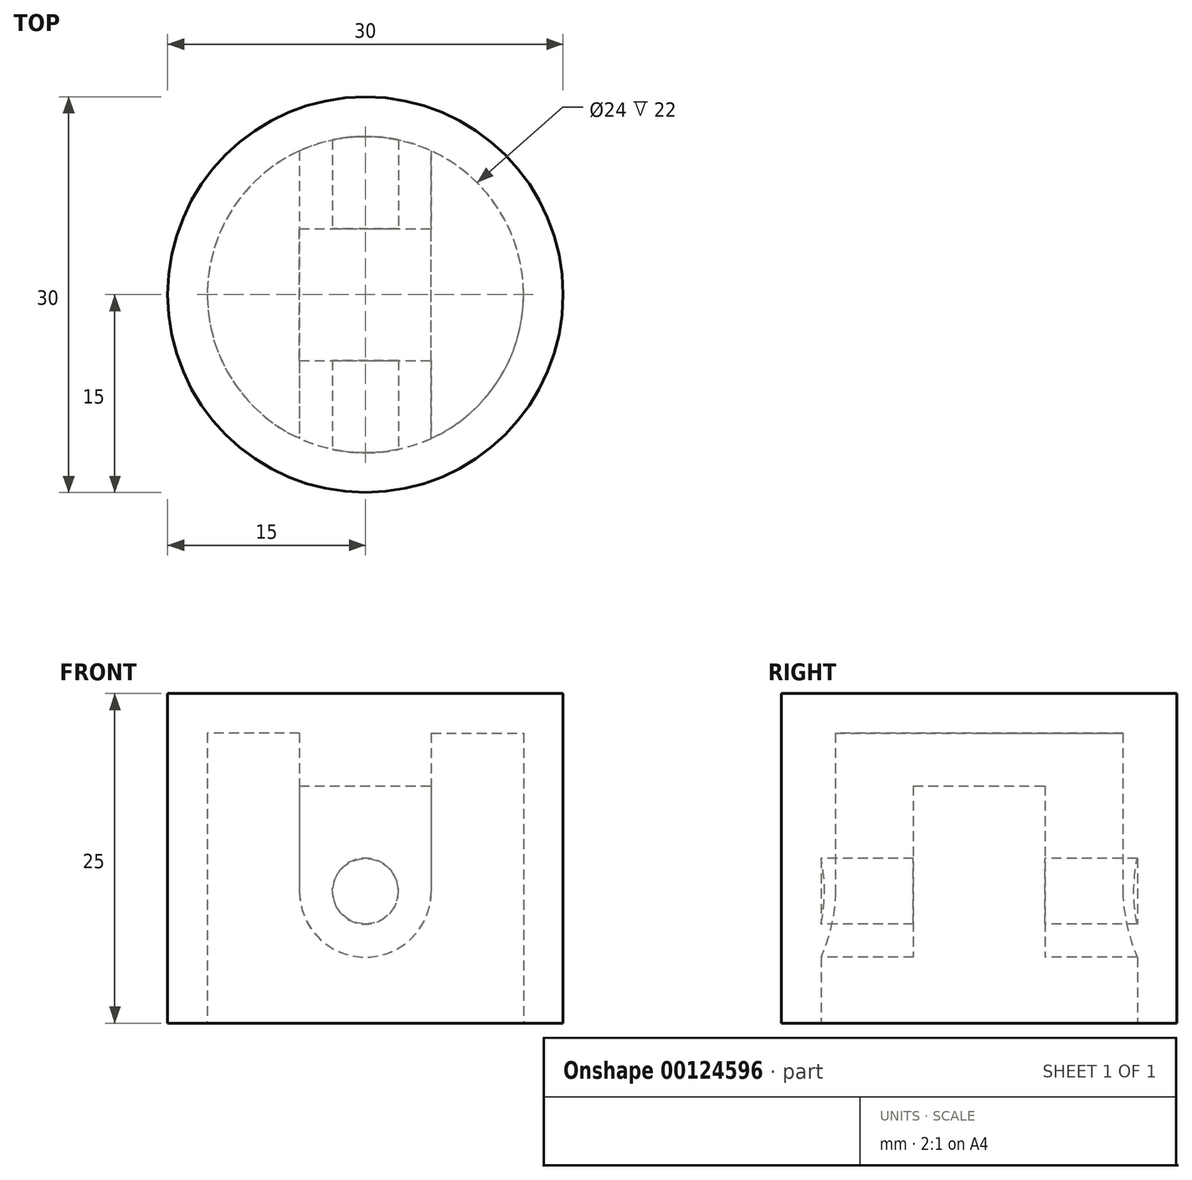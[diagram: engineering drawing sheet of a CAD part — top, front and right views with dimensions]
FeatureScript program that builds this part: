
annotation { "Feature Type Name" : "Feature", "Feature Type Description" : "" }
export const myFeature = defineFeature(function(context is Context, id is Id, definition is map)
    precondition{}
    {
        {
            var Q0;
            Q0=qCreatedBy(makeId("Front.planeOp"),FACE);
            var sketch = newSketch(context, id + "F0", { "sketchPlane" : qUnion([Q0])});
            skLineSegment(sketch, "E0", {"start": v(-38.21, 50) * mm, "end": v(61.79, 50) * mm, "construction": true});
            skLineSegment(sketch, "E1", {"start": v(-41.68, 90) * mm, "end": v(52.02, 90) * mm, "construction": true});
            skLineSegment(sketch, "E2", {"start": v(0, 0) * mm, "end": v(0, 124.4) * mm, "construction": true});
            skLineSegment(sketch, "E3", {"start": v(0, 0) * mm, "end": v(-17.32, 10) * mm});
            skLineSegment(sketch, "E4", {"start": v(-17.32, 10) * mm, "end": v(0, 62.2) * mm});
            skLineSegment(sketch, "E5", {"start": v(-60.14, 0) * mm, "end": v(58.23, 0) * mm, "construction": true});
            skLineSegment(sketch, "E6.bottom", {"start": v(-15, 77.2) * mm, "end": v(15, 77.2) * mm});
            skLineSegment(sketch, "E6.top", {"start": v(-15, 52.2) * mm, "end": v(15, 52.2) * mm});
            skLineSegment(sketch, "E6.left", {"start": v(-15, 52.2) * mm, "end": v(-15, 77.2) * mm});
            skLineSegment(sketch, "E6.right", {"start": v(15, 52.2) * mm, "end": v(15, 77.2) * mm});
            skLineSegment(sketch, "E7", {"start": v(-5, 77.2) * mm, "end": v(-5, 70.2) * mm});
            skLineSegment(sketch, "E8", {"start": v(-5, 70.2) * mm, "end": v(-5, 62.2) * mm});
            skLineSegment(sketch, "E9", {"start": v(5, 70.2) * mm, "end": v(5, 62.2) * mm});
            skArc(sketch, "E10", {"start": v(-5, 62.2) * mm, "mid": v(0, 57.2) * mm, "end": v(5, 62.2) * mm});
            skLineSegment(sketch, "E11", {"start": v(5, 70.2) * mm, "end": v(5, 77.2) * mm});
            skLineSegment(sketch, "E12", {"start": v(-5, 70.2) * mm, "end": v(5, 70.2) * mm});
            skCircle(sketch, "E13", {"center": v(0, 62.2) * mm, "radius": 2.5 * mm});
            skSolve(sketch);
        }
        {
            var Q0;
            Q0=qCreatedBy(makeId("Front.planeOp"),FACE);
            var sketch = newSketch(context, id + "F1", { "sketchPlane" : qUnion([Q0])});
            skLineSegment(sketch, "E14.0", {"start": v(0, 77.2) * mm, "end": v(15, 77.2) * mm});
            skLineSegment(sketch, "E15.0", {"start": v(15, 52.2) * mm, "end": v(15, 77.2) * mm});
            skLineSegment(sketch, "E16.0", {"start": v(0, 52.2) * mm, "end": v(15, 52.2) * mm});
            skLineSegment(sketch, "E17.0", {"start": v(0, 0) * mm, "end": v(0, 124.4) * mm});
            skPoint(sketch, "E18.orphan", {"position": v(-15, 77.2) * mm});
            skPoint(sketch, "E19.orphan", {"position": v(-15, 52.2) * mm});
            skSolve(sketch);
        }
        {
            var Q0;
            {var subQ0=sQuery(id+"F1.wireOp",EDGE,"E14.0");Q0=makeQuery(id+"F1.imprint","IMPRINT",FACE,{"disambiguationData":[TD([[makeQuery(id+"F1.imprint","IMPRINT",EDGE,{"derivedFrom":subQ0}),-1.0]])]});}
            var Q1;
            Q1=sQuery(id+"F1.wireOp",EDGE,"E17.0");
            revolve(context, id + "F2", {"entities" : qUnion([Q0]), "axis" : qUnion([Q1]), "revolveType" : RevolveType.FULL});
        }
        {
            var Q0;
            Q0=makeQuery(id+"F2.opRevolve","SWEPT_FACE",FACE,{"disambiguationData":[OSD([sQuery(id+"F1.wireOp",EDGE,"E16.0")])]});
            shell(context, id + "F3", {"entities" : qUnion([Q0]), "thickness" : 3 * mm});
        }
        {
            var Q0;
            {var subQ3=sQuery(id+"F0.wireOp",EDGE,"E8");Q0=makeQuery(id+"F0.imprint","IMPRINT",FACE,{"disambiguationData":[TD([[makeQuery(id+"F0.imprint","IMPRINT",EDGE,{"derivedFrom":subQ3}),1.0]])]});}
            extrude(context, id + "F4", {"entities" : qUnion([Q0]), "operationType" : NewBodyOperationType.ADD, "endBound" : BoundingType.UP_TO_NEXT, "oppositeDirection" : true, "depth" : 10 * mm, "hasSecondDirection" : true, "secondDirectionBound" : SecondDirectionBoundingType.UP_TO_NEXT, "secondDirectionOppositeDirection" : false, "secondDirectionDepth" : 10 * mm});
        }
        {
            var Q0;
            Q0=qCreatedBy(makeId("Front.planeOp"),FACE);
            var sketch = newSketch(context, id + "F5", { "sketchPlane" : qUnion([Q0])});
            skLineSegment(sketch, "E20", {"start": v(-5, 70.2) * mm, "end": v(-5, 62.2) * mm});
            skLineSegment(sketch, "E21", {"start": v(-5, 70.2) * mm, "end": v(5, 70.2) * mm});
            skLineSegment(sketch, "E22", {"start": v(5, 70.2) * mm, "end": v(5, 62.2) * mm});
            skArc(sketch, "E23", {"start": v(-5, 62.2) * mm, "mid": v(0, 57.2) * mm, "end": v(5, 62.2) * mm});
            skCircle(sketch, "E24", {"center": v(0, 62.2) * mm, "radius": 2.5 * mm});
            skSolve(sketch);
        }
        {
            var Q0;
            Q0=qSketchRegion(id+"F5",true);
            extrude(context, id + "F6", {"entities" : qUnion([Q0]), "operationType" : NewBodyOperationType.REMOVE, "endBound" : BoundingType.SYMMETRIC, "depth" : 10 * mm});
        }
        {
            var Q0;
            Q0=qCreatedBy(makeId("Front.planeOp"),FACE);
            var sketch = newSketch(context, id + "F7", { "sketchPlane" : qUnion([Q0])});
            skLineSegment(sketch, "E25", {"start": v(-5, 77.2) * mm, "end": v(-5, 70.2) * mm});
            skLineSegment(sketch, "E26", {"start": v(-5, 70.2) * mm, "end": v(5, 70.2) * mm});
            skLineSegment(sketch, "E27", {"start": v(5, 70.2) * mm, "end": v(5, 77.2) * mm});
            skLineSegment(sketch, "E28", {"start": v(5, 77.2) * mm, "end": v(-5, 77.2) * mm});
            skSolve(sketch);
        }
        {
            var Q0;
            Q0=qSketchRegion(id+"F7",true);
            extrude(context, id + "F8", {"entities" : qUnion([Q0]), "operationType" : NewBodyOperationType.ADD, "endBound" : BoundingType.UP_TO_NEXT, "depth" : 10.15 * mm, "hasSecondDirection" : true, "secondDirectionBound" : SecondDirectionBoundingType.UP_TO_NEXT, "secondDirectionOppositeDirection" : true, "secondDirectionDepth" : 4.75 * mm});
        }
    });
